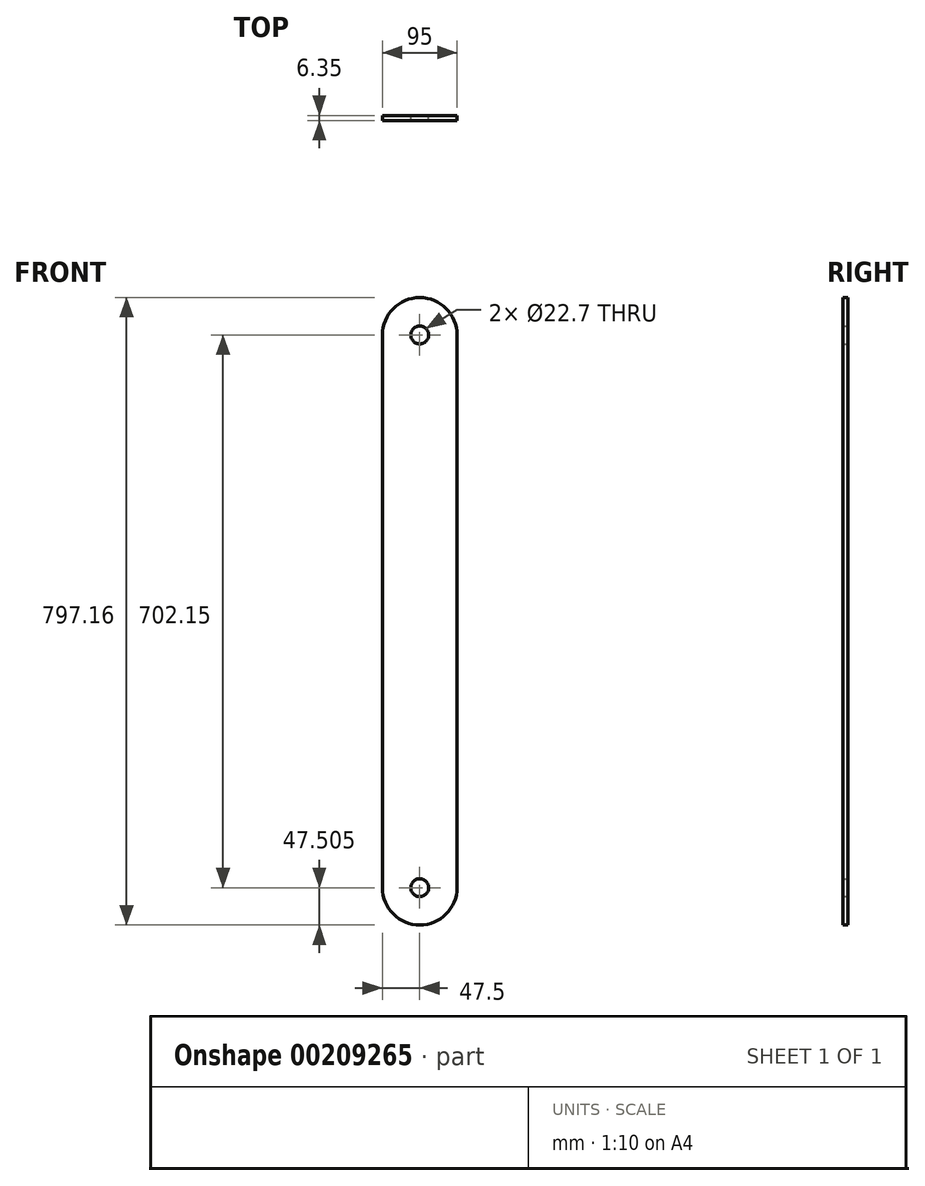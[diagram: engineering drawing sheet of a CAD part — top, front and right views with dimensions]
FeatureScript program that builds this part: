
annotation { "Feature Type Name" : "Feature", "Feature Type Description" : "" }
export const myFeature = defineFeature(function(context is Context, id is Id, definition is map)
    precondition{}
    {
        {
            var Q0;
            Q0=qCreatedBy(makeId("Front.planeOp"),FACE);
            var sketch = newSketch(context, id + "F0", { "sketchPlane" : qUnion([Q0])});
            skArc(sketch, "E0", {"start": v(47.5, 351.07) * mm, "mid": v(0, 398.57) * mm, "end": v(-47.5, 351.07) * mm});
            skLineSegment(sketch, "E1", {"start": v(47.5, 351.07) * mm, "end": v(47.5, -351.07) * mm});
            skArc(sketch, "E2", {"start": v(-47.5, -351.07) * mm, "mid": v(0, -398.57) * mm, "end": v(47.5, -351.07) * mm});
            skLineSegment(sketch, "E3", {"start": v(-47.5, 351.08) * mm, "end": v(-47.5, -351.07) * mm});
            skCircle(sketch, "E4", {"center": v(0, 351.07) * mm, "radius": 11.35 * mm});
            skCircle(sketch, "E5", {"center": v(0, -351.07) * mm, "radius": 11.35 * mm});
            skSolve(sketch);
        }
        {
            var Q0;
            Q0=qSketchRegion(id+"F0",true);
            extrude(context, id + "F1", {"entities" : qUnion([Q0]), "depth" : 6.35 * mm});
        }
    });
